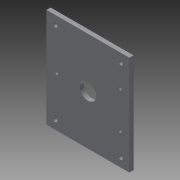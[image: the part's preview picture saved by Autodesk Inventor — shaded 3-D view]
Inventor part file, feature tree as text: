
AUTODESK INVENTOR PART (.ipt)
format: ipt  version: 2014 SP1 (Build 180222100, 222)  size: 103,424 bytes
history: native  units: in
note: dims shown in document units (in); Inventor stores cm internally (conversion verified against a paired STEP export)
features: extrude x1, sketch x1
ambient origin geometry x8: Origin, YZ Plane, XZ Plane, XY Plane, X Axis, Y Axis, Z Axis, Center Point
bodies: Solid1 (feature_tree)
feature tree (2):
  extrude  "Extrusion1"  Depth=6.0in
  sketch  "Sketch1"  dims[d0=5.0in d1=6.0in d2=0.75in d3=45.0deg d6=0.25in d7=0.25in d8=0.25in d9=0.25in d10=1.0in d11=1.9055in d12=1.9291in d13=1.1138in d14=1.1138in d15=0.189in d16=0.189in d17=0.189in d18=0.25in d19=0.0in]
